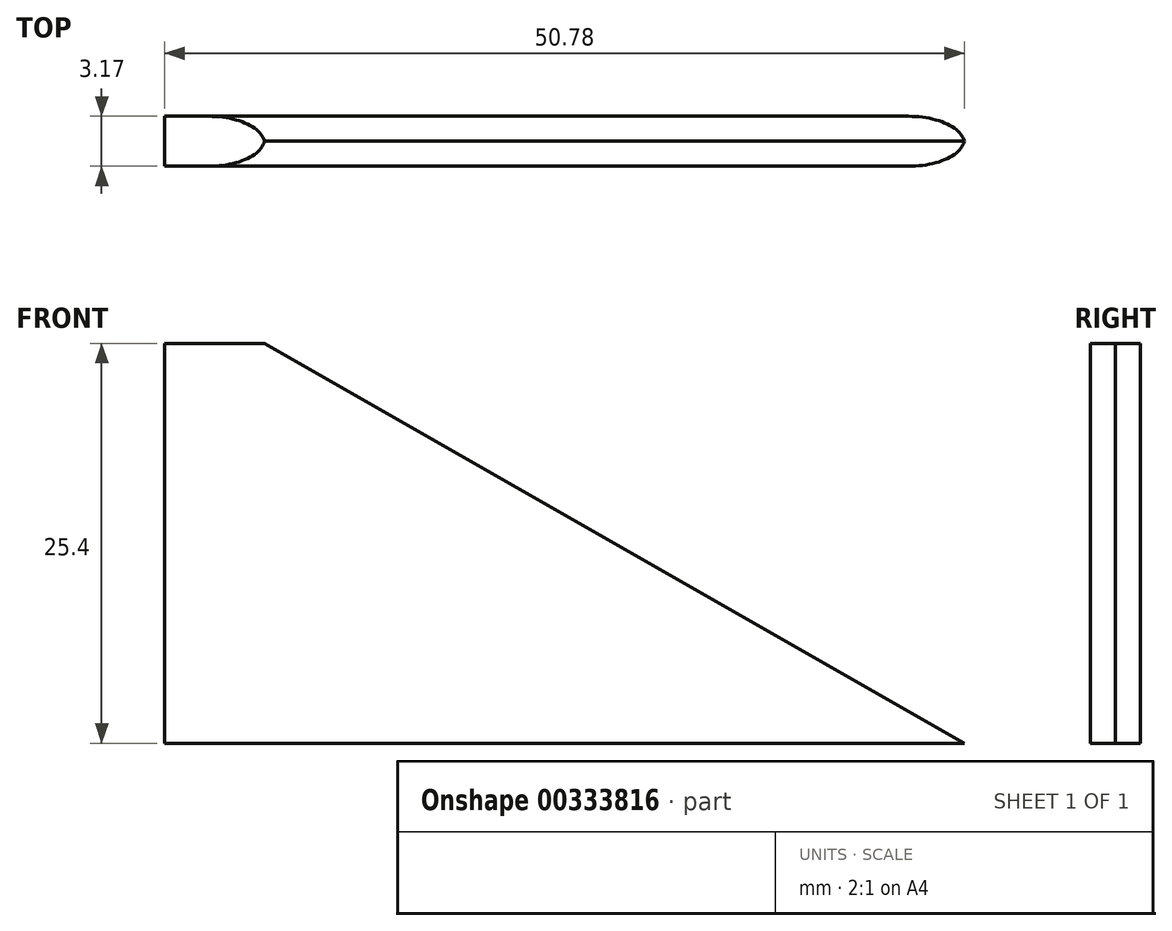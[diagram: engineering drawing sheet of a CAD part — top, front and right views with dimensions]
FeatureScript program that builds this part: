
annotation { "Feature Type Name" : "Feature", "Feature Type Description" : "" }
export const myFeature = defineFeature(function(context is Context, id is Id, definition is map)
    precondition{}
    {
        {
            var Q0;
            Q0=qCreatedBy(makeId("Front.planeOp"),FACE);
            var sketch = newSketch(context, id + "F0", { "sketchPlane" : qUnion([Q0])});
            skLineSegment(sketch, "E0", {"start": v(0, 0) * mm, "end": v(50.8, 0) * mm});
            skLineSegment(sketch, "E1", {"start": v(50.8, 0) * mm, "end": v(6.35, 25.4) * mm});
            skLineSegment(sketch, "E2", {"start": v(6.35, 25.4) * mm, "end": v(0, 25.4) * mm});
            skLineSegment(sketch, "E3", {"start": v(0, 25.4) * mm, "end": v(0, 0) * mm});
            skSolve(sketch);
        }
        {
            var Q0;
            Q0 = qSketchRegion(id + "F0", true);
            extrude(context, id + "F1", {"entities" : qUnion([Q0]), "depth" : 3.17 * mm});
        }
        {
            var Q0;
            Q0=makeQuery(id+"F1.opExtrude","CAP_EDGE",EDGE,{"disambiguationData":[OSD([sQuery(id+"F0.wireOp",EDGE,"E1")])],"isStart":false});
            var Q1;
            Q1=makeQuery(id+"F1.opExtrude","CAP_EDGE",EDGE,{"disambiguationData":[OSD([sQuery(id+"F0.wireOp",EDGE,"E1")])],"isStart":true});
            fillet(context, id + "F2", {"entities" : qUnion([Q0, Q1]), "radius" : 1.78 * mm, "tangentPropagation" : true, "allowEdgeOverflow" : false});
        }
    });
